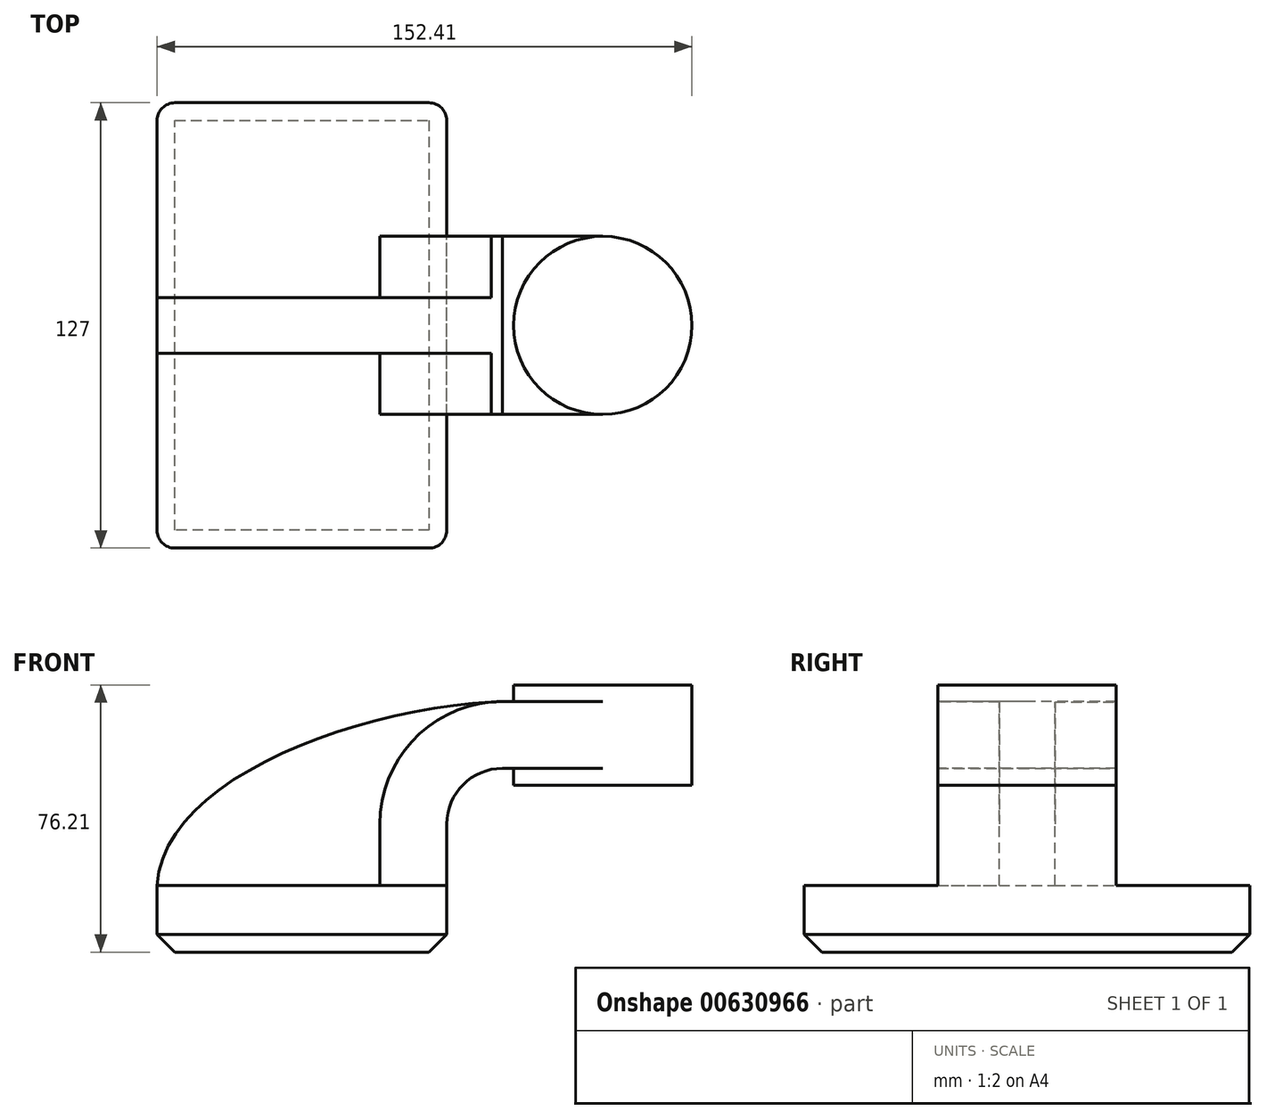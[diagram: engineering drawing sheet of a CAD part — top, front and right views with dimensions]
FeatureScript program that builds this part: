
annotation { "Feature Type Name" : "Feature", "Feature Type Description" : "" }
export const myFeature = defineFeature(function(context is Context, id is Id, definition is map)
    precondition{}
    {
        {
            var Q0;
            Q0=qCreatedBy(makeId("Front.planeOp"),FACE);
            var sketch = newSketch(context, id + "F0", { "sketchPlane" : qUnion([Q0])});
            skLineSegment(sketch, "E0.rect.bottom", {"start": v(-41.28, 9.52) * mm, "end": v(41.28, 9.52) * mm});
            skLineSegment(sketch, "E0.rect.top", {"start": v(-41.28, -9.52) * mm, "end": v(41.28, -9.52) * mm});
            skLineSegment(sketch, "E0.rect.left", {"start": v(-41.28, 9.52) * mm, "end": v(-41.28, -9.52) * mm});
            skLineSegment(sketch, "E0.rect.right", {"start": v(41.28, 9.52) * mm, "end": v(41.28, -9.52) * mm});
            skPoint(sketch, "E0.rect.middle", {"position": v(0, 0) * mm});
            skLineSegment(sketch, "E1", {"start": v(41.28, 9.52) * mm, "end": v(41.28, 27) * mm});
            skArc(sketch, "E2", {"start": v(41.28, 27) * mm, "mid": v(45.92, 38.23) * mm, "end": v(57.15, 42.88) * mm});
            skLineSegment(sketch, "E3", {"start": v(57.15, 42.88) * mm, "end": v(85.72, 42.88) * mm});
            skLineSegment(sketch, "E4.rect.bottom", {"start": v(60.32, 38.1) * mm, "end": v(111.12, 38.1) * mm});
            skLineSegment(sketch, "E4.rect.top", {"start": v(60.32, 66.68) * mm, "end": v(111.12, 66.68) * mm});
            skLineSegment(sketch, "E4.rect.left", {"start": v(60.32, 38.1) * mm, "end": v(60.32, 66.68) * mm});
            skLineSegment(sketch, "E4.rect.right", {"start": v(111.13, 38.1) * mm, "end": v(111.12, 66.68) * mm});
            skPoint(sketch, "E4.rect.middle", {"position": v(85.72, 52.39) * mm});
            skLineSegment(sketch, "E5.0", {"start": v(57.15, 61.93) * mm, "end": v(85.72, 61.93) * mm});
            skArc(sketch, "E5.1", {"start": v(22.23, 27) * mm, "mid": v(32.45, 51.7) * mm, "end": v(57.15, 61.93) * mm});
            skLineSegment(sketch, "E5.2", {"start": v(22.23, 9.52) * mm, "end": v(22.23, 27) * mm});
            skLineSegment(sketch, "E6", {"start": v(85.72, 38.1) * mm, "end": v(85.72, 66.68) * mm});
            skFitSpline(sketch, "E7", {"points": [v(-41.28, 9.53) * mm, v(57.15, 61.93) * mm], "startDerivative": vector(5.2, 92.34) * mm, "endDerivative": vector(120.92, 4.22) * mm});
            skSolve(sketch);
        }
        {
            var Q0;
            Q0=makeQuery(id+"F0.imprint","IMPRINT",FACE,{"disambiguationData":[TD([[makeQuery(id+"F0.imprint","IMPRINT",EDGE,{"derivedFrom":sQuery(id+"F0.wireOp",EDGE,"E0.rect.top")}),1.0]])]});
            extrude(context, id + "F1", {"entities" : qUnion([Q0]), "endBound" : BoundingType.SYMMETRIC, "depth" : 127 * mm});
        }
        {
            var Q0;
            {var subQ9=sQuery(id+"F0.wireOp",EDGE,"E1");Q0=makeQuery(id+"F0.imprint","IMPRINT",FACE,{"disambiguationData":[TD([[makeQuery(id+"F0.imprint","IMPRINT",EDGE,{"derivedFrom":subQ9}),1.0]])]});}
            var Q1;
            {var subQ0=sQuery(id+"F0.wireOp",EDGE,"E6");var subQ1=sQuery(id+"F0.wireOp",EDGE,"E3");var subQ2=makeQuery(id+"F0.imprint","INTERSECT",VERTEX,{"derivedFrom":[subQ1,subQ0]});Q1=makeQuery(id+"F0.imprint","IMPRINT",FACE,{"disambiguationData":[TD([[makeQuery(id+"F0.imprint","IMPRINT",EDGE,{"disambiguationData":[TD([[subQ2,1.0]])],"derivedFrom":subQ1}),1.0]])]});}
            extrude(context, id + "F2", {"entities" : qUnion([Q0, Q1]), "operationType" : NewBodyOperationType.ADD, "endBound" : BoundingType.SYMMETRIC, "depth" : 50.8 * mm});
        }
        {
            var Q0;
            {var subQ3=sQuery(id+"F0.wireOp",EDGE,"E5.2");Q0=makeQuery(id+"F0.imprint","IMPRINT",FACE,{"disambiguationData":[TD([[makeQuery(id+"F0.imprint","IMPRINT",EDGE,{"derivedFrom":subQ3}),1.0]])]});}
            extrude(context, id + "F3", {"entities" : qUnion([Q0]), "operationType" : NewBodyOperationType.ADD, "endBound" : BoundingType.SYMMETRIC, "depth" : 15.88 * mm});
        }
        {
            var Q0;
            {var subQ5=sQuery(id+"F0.wireOp",EDGE,"E4.rect.right");Q0=makeQuery(id+"F0.imprint","IMPRINT",FACE,{"disambiguationData":[TD([[makeQuery(id+"F0.imprint","IMPRINT",EDGE,{"derivedFrom":subQ5}),1.0]])]});}
            var Q1;
            Q1=sQuery(id+"F0.wireOp",EDGE,"E6");
            revolve(context, id + "F4", {"operationType" : NewBodyOperationType.ADD, "entities" : qUnion([Q0]), "axis" : qUnion([Q1]), "revolveType" : RevolveType.FULL});
        }
        {
            var Q0;
            Q0=makeQuery(id+"F1.opExtrude","CAP_EDGE",EDGE,{"disambiguationData":[OSD([sQuery(id+"F0.wireOp",EDGE,"E0.rect.right")])],"isStart":false});
            var Q1;
            Q1=makeQuery(id+"F1.opExtrude","CAP_EDGE",EDGE,{"disambiguationData":[OSD([sQuery(id+"F0.wireOp",EDGE,"E0.rect.left")])],"isStart":false});
            var Q2;
            Q2=makeQuery(id+"F1.opExtrude","CAP_EDGE",EDGE,{"disambiguationData":[OSD([sQuery(id+"F0.wireOp",EDGE,"E0.rect.right")])],"isStart":true});
            var Q3;
            Q3=makeQuery(id+"F1.opExtrude","CAP_EDGE",EDGE,{"disambiguationData":[OSD([sQuery(id+"F0.wireOp",EDGE,"E0.rect.left")])],"isStart":true});
            fillet(context, id + "F5", {"entities" : qUnion([Q0, Q1, Q2, Q3]), "radius" : 5.08 * mm, "tangentPropagation" : true, "allowEdgeOverflow" : false});
        }
        {
            var Q0;
            Q0=makeQuery(id+"F5.opFillet","BLEND_EDGE",EDGE,{"blendedFrom":[makeQuery(id+"F1.opExtrude","CAP_EDGE",EDGE,{"disambiguationData":[OSD([sQuery(id+"F0.wireOp",EDGE,"E0.rect.left")])],"isStart":false}),makeQuery(id+"F1.opExtrude","SWEPT_FACE",FACE,{"disambiguationData":[OSD([sQuery(id+"F0.wireOp",EDGE,"E0.rect.top")])]})],"blendedInto":[makeQuery(id+"F1.opExtrude","SWEPT_FACE",FACE,{"disambiguationData":[OSD([sQuery(id+"F0.wireOp",EDGE,"E0.rect.top")])]})]});
            chamfer(context, id + "F6", {"entities" : qUnion([Q0]), "width" : 5.08 * mm, "tangentPropagation" : true});
        }
    });
